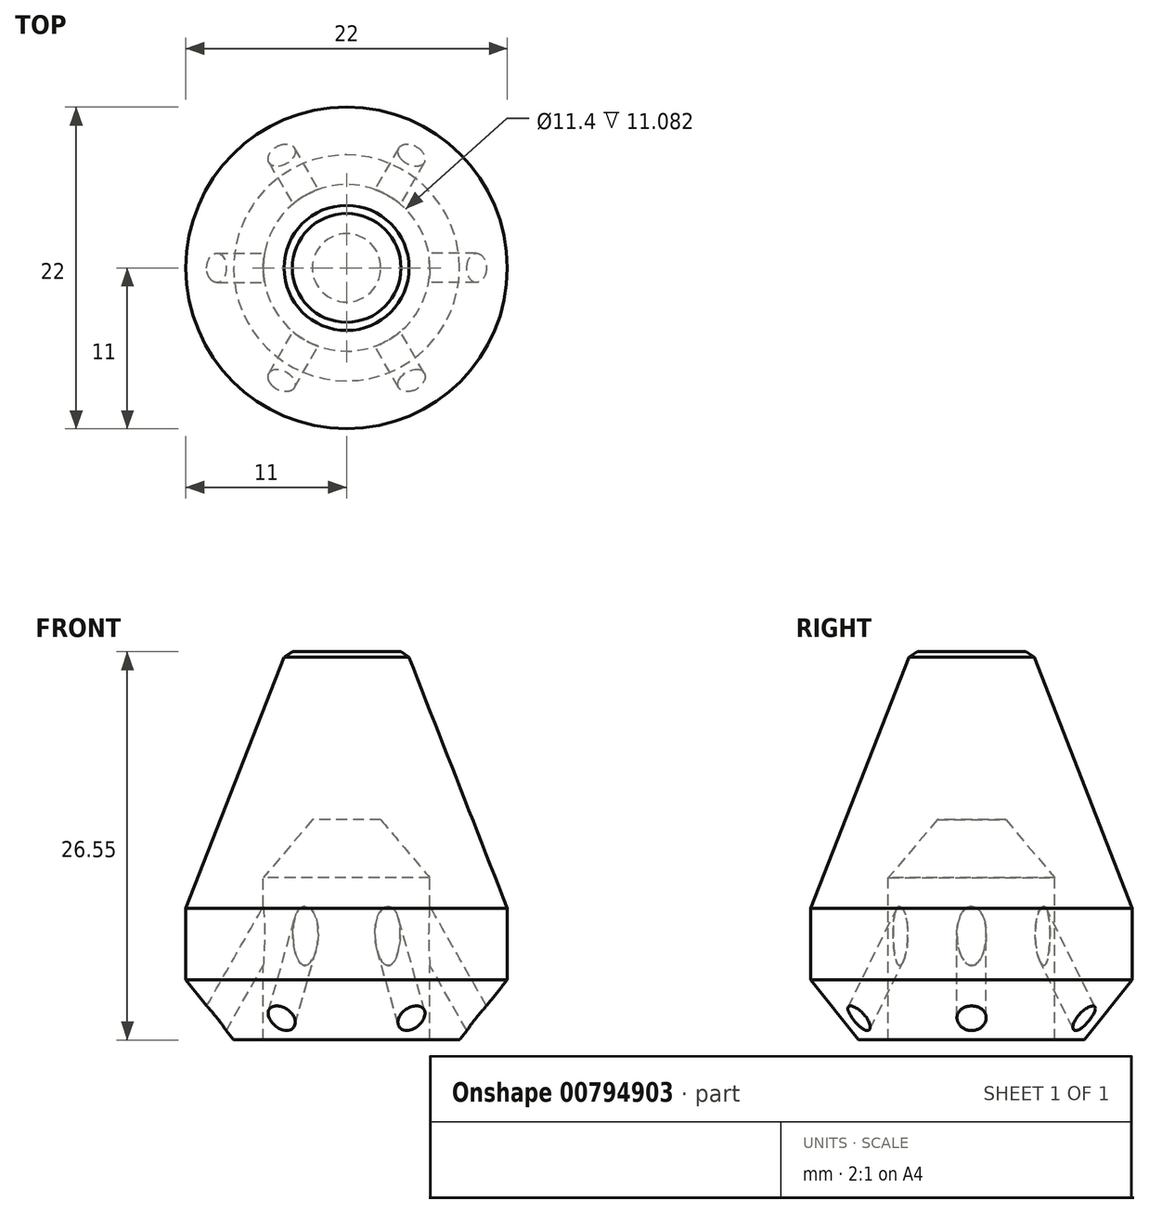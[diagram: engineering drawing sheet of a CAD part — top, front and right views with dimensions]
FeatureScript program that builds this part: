
annotation { "Feature Type Name" : "Feature", "Feature Type Description" : "" }
export const myFeature = defineFeature(function(context is Context, id is Id, definition is map)
    precondition{}
    {
        {
            var Q0;
            Q0=qCreatedBy(makeId("Front.planeOp"),FACE);
            var sketch = newSketch(context, id + "F0", { "sketchPlane" : qUnion([Q0])});
            skLineSegment(sketch, "E0", {"start": v(5.7, -6.95) * mm, "end": v(5.7, 2.79) * mm});
            skLineSegment(sketch, "E1", {"start": v(7.73, -8.3) * mm, "end": v(11, -4.18) * mm});
            skLineSegment(sketch, "E2", {"start": v(11, -4.18) * mm, "end": v(11, 0.7) * mm});
            skLineSegment(sketch, "E3", {"start": v(0, 6.76) * mm, "end": v(2.34, 6.76) * mm});
            skLineSegment(sketch, "E4", {"start": v(2.34, 6.76) * mm, "end": v(5.7, 2.79) * mm});
            skLineSegment(sketch, "E5", {"start": v(0, 18.25) * mm, "end": v(0, 6.76) * mm});
            skLineSegment(sketch, "E6", {"start": v(11, 0.7) * mm, "end": v(4.13, 18.25) * mm});
            skLineSegment(sketch, "E7", {"start": v(4.13, 18.25) * mm, "end": v(0, 18.25) * mm});
            skLineSegment(sketch, "E8", {"start": v(5.7, -6.95) * mm, "end": v(5.7, -8.3) * mm});
            skLineSegment(sketch, "E9", {"start": v(5.7, -8.3) * mm, "end": v(7.73, -8.3) * mm});
            skSolve(sketch);
        }
        {
            var Q0;
            Q0 = qSketchRegion(id + "F0", true);
            var Q1;
            Q1=sQuery(id+"F0.wireOp",EDGE,"E5");
            revolve(context, id + "F1", {"surfaceOperationType" : NewSurfaceOperationType.NEW, "entities" : qUnion([Q0]), "axis" : qUnion([Q1]), "revolveType" : RevolveType.FULL});
        }
        {
            var Q0;
            Q0=qCreatedBy(makeId("Front.planeOp"),FACE);
            var sketch = newSketch(context, id + "F2", { "sketchPlane" : qUnion([Q0])});
            skLineSegment(sketch, "E10", {"start": v(16.57, -18.26) * mm, "end": v(4.6, 2.78) * mm});
            skLineSegment(sketch, "E11", {"start": v(4.6, 2.78) * mm, "end": v(3.72, 2.28) * mm});
            skLineSegment(sketch, "E12", {"start": v(3.72, 2.28) * mm, "end": v(15.92, -19.14) * mm});
            skLineSegment(sketch, "E13", {"start": v(15.92, -19.14) * mm, "end": v(16.57, -18.26) * mm});
            skSolve(sketch);
        }
        {
            var Q0;
            Q0 = qSketchRegion(id + "F2", true);
            var Q1;
            Q1=sQuery(id+"F2.wireOp",EDGE,"E12");
            revolve(context, id + "F3", {"surfaceOperationType" : NewSurfaceOperationType.NEW, "entities" : qUnion([Q0]), "axis" : qUnion([Q1]), "revolveType" : RevolveType.FULL});
        }
        {
            var Q0;
            Q0=makeQuery(id+"F3.opRevolve","SWEPT_BODY",BODY,{"disambiguationData":[OSD([sQuery(id+"F2.wireOp",EDGE,"E10"),sQuery(id+"F2.wireOp",EDGE,"E11"),sQuery(id+"F2.wireOp",EDGE,"E12"),sQuery(id+"F2.wireOp",EDGE,"E13")])]});
            var Q1;
            Q1=sQuery(id+"F0.wireOp",EDGE,"E5");
            circularPattern(context, id + "F4", {"operationType" : NewBodyOperationType.REMOVE, "entities" : qUnion([Q0]), "axis" : qUnion([Q1]), "angle" : 360 * degree, "instanceCount" : 6, "equalSpace" : true});
        }
        {
            var Q0;
            Q0=makeQuery(id+"F1.opRevolve","SWEPT_EDGE",EDGE,{"disambiguationData":[OSD([sQuery(id+"F0.wireOp",EDGE,"E6"),sQuery(id+"F0.wireOp",EDGE,"E7")])]});
            chamfer(context, id + "F5", {"entities" : qUnion([Q0]), "width" : 0.6 * mm, "tangentPropagation" : true});
        }
    });
